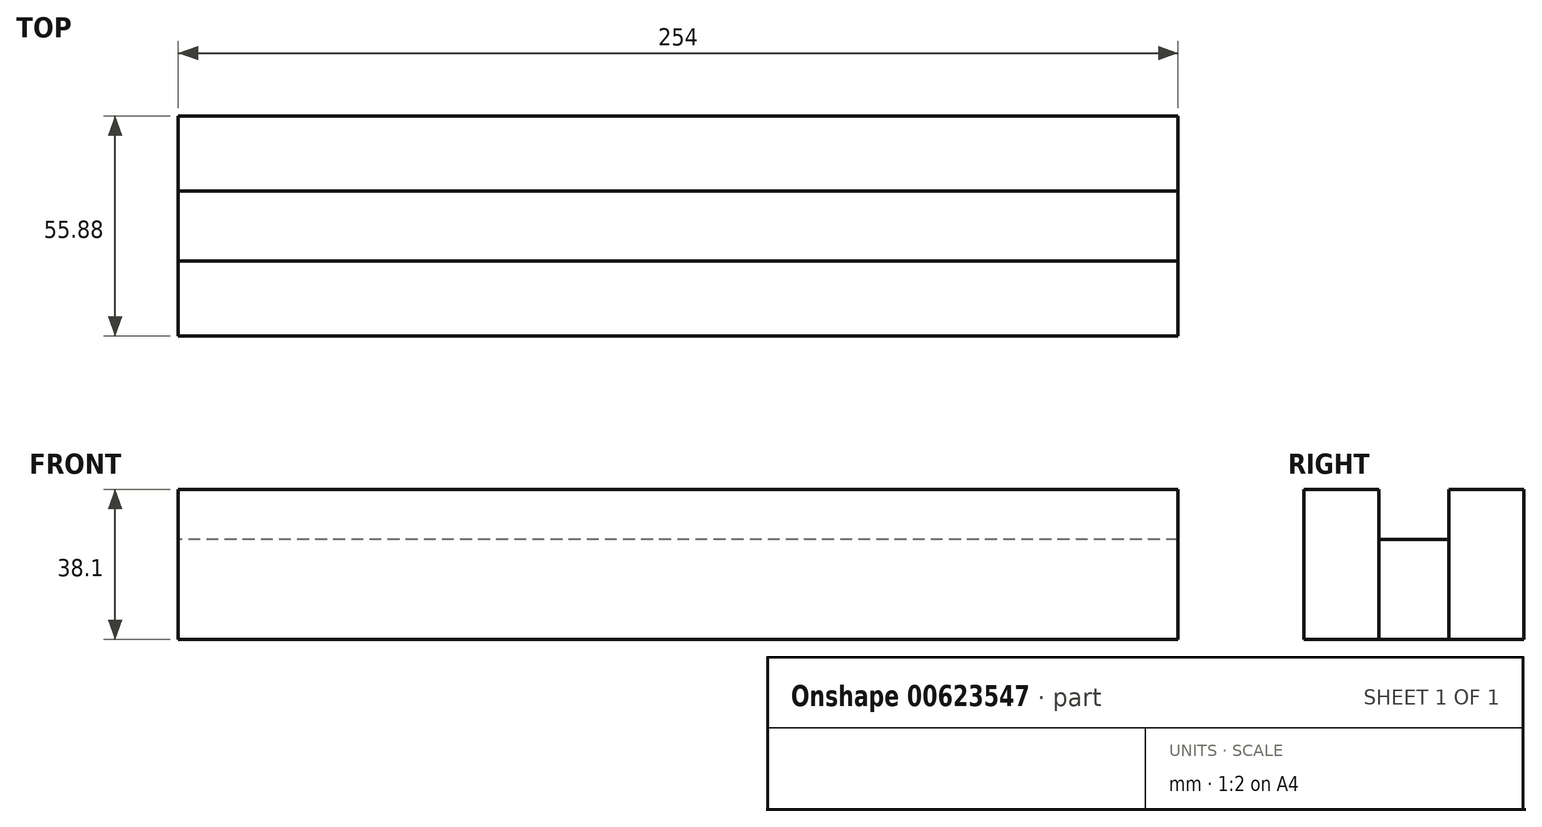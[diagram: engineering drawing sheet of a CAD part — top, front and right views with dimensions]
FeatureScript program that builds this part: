
annotation { "Feature Type Name" : "Feature", "Feature Type Description" : "" }
export const myFeature = defineFeature(function(context is Context, id is Id, definition is map)
    precondition{}
    {
        {
            var Q0;
            Q0=qCreatedBy(makeId("Right.planeOp"),FACE);
            var sketch = newSketch(context, id + "F0", { "sketchPlane" : qUnion([Q0])});
            skLineSegment(sketch, "E0.bottom", {"start": v(8.9, -12.7) * mm, "end": v(-8.9, -12.7) * mm});
            skLineSegment(sketch, "E0.top", {"start": v(8.9, 12.7) * mm, "end": v(-8.89, 12.7) * mm});
            skLineSegment(sketch, "E0.left", {"start": v(8.9, -12.7) * mm, "end": v(8.9, 12.7) * mm});
            skLineSegment(sketch, "E0.right", {"start": v(-8.9, -12.7) * mm, "end": v(-8.89, 12.7) * mm});
            skPoint(sketch, "E0.middle", {"position": v(0, 0) * mm});
            skLineSegment(sketch, "E1.bottom", {"start": v(8.9, -12.7) * mm, "end": v(27.94, -12.7) * mm});
            skLineSegment(sketch, "E1.top", {"start": v(8.89, 25.4) * mm, "end": v(27.94, 25.4) * mm});
            skLineSegment(sketch, "E1.left", {"start": v(8.9, -12.7) * mm, "end": v(8.9, 25.4) * mm});
            skLineSegment(sketch, "E1.right", {"start": v(27.94, -12.7) * mm, "end": v(27.94, 25.4) * mm});
            skLineSegment(sketch, "E2.bottom", {"start": v(-8.9, -12.7) * mm, "end": v(-27.94, -12.7) * mm});
            skLineSegment(sketch, "E2.top", {"start": v(-8.9, 25.4) * mm, "end": v(-27.94, 25.4) * mm});
            skLineSegment(sketch, "E2.left", {"start": v(-8.9, -12.7) * mm, "end": v(-8.9, 25.4) * mm});
            skLineSegment(sketch, "E2.right", {"start": v(-27.94, -12.7) * mm, "end": v(-27.94, 25.4) * mm});
            skSolve(sketch);
        }
        {
            var Q0;
            {var subQ0=sQuery(id+"F0.wireOp",EDGE,"E0.bottom");Q0=makeQuery(id+"F0.imprint","IMPRINT",FACE,{"disambiguationData":[TD([[makeQuery(id+"F0.imprint","IMPRINT",EDGE,{"derivedFrom":subQ0}),-1.0]])]});}
            extrude(context, id + "F1", {"entities" : qUnion([Q0]), "depth" : 254 * mm, "offsetDistance" : 25.4 * mm});
        }
        {
            var Q0;
            {var subQ3=sQuery(id+"F0.wireOp",EDGE,"E2.bottom");Q0=makeQuery(id+"F0.imprint","IMPRINT",FACE,{"disambiguationData":[TD([[makeQuery(id+"F0.imprint","IMPRINT",EDGE,{"derivedFrom":subQ3}),-1.0]])]});}
            var Q1;
            {var subQ3=sQuery(id+"F0.wireOp",EDGE,"E1.bottom");Q1=makeQuery(id+"F0.imprint","IMPRINT",FACE,{"disambiguationData":[TD([[makeQuery(id+"F0.imprint","IMPRINT",EDGE,{"derivedFrom":subQ3}),1.0]])]});}
            extrude(context, id + "F2", {"entities" : qUnion([Q0, Q1]), "depth" : 254 * mm, "offsetDistance" : 25.4 * mm});
        }
    });
